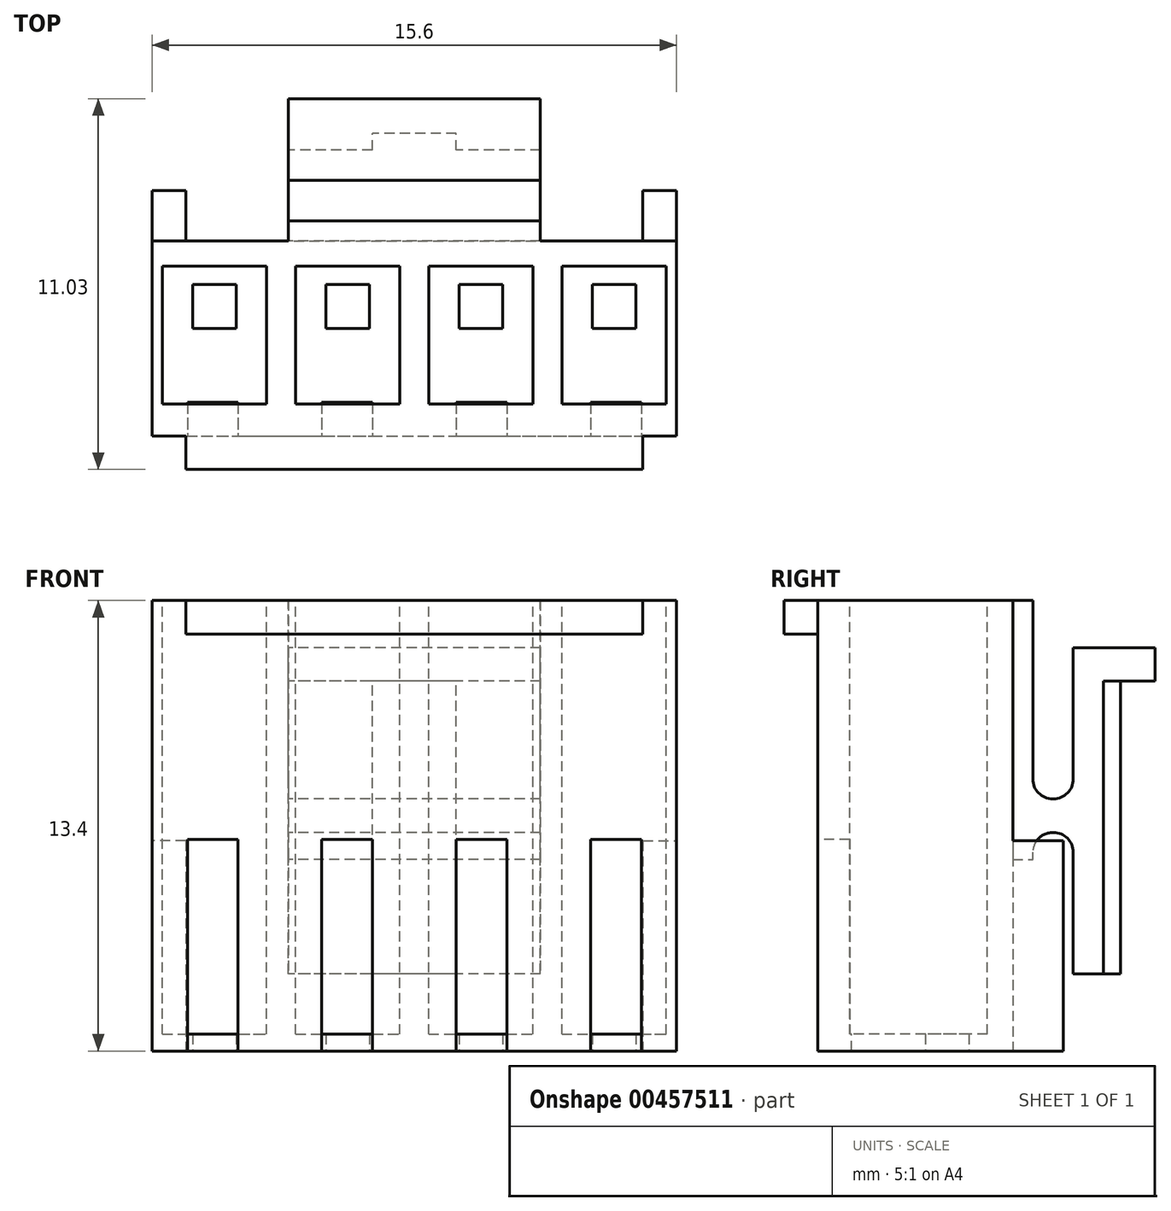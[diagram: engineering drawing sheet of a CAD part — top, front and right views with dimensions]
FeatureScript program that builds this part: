
annotation { "Feature Type Name" : "Feature", "Feature Type Description" : "" }
export const myFeature = defineFeature(function(context is Context, id is Id, definition is map)
    precondition{}
    {
        {
            var Q0;
            Q0=qCreatedBy(makeId("Top.planeOp"),FACE);
            var sketch = newSketch(context, id + "F0", { "sketchPlane" : qUnion([Q0])});
            skLineSegment(sketch, "E0.bottom", {"start": v(-7.8, 2.9) * mm, "end": v(7.8, 2.9) * mm});
            skLineSegment(sketch, "E0.top", {"start": v(-7.8, -2.9) * mm, "end": v(7.8, -2.9) * mm});
            skLineSegment(sketch, "E0.left", {"start": v(-7.8, 2.9) * mm, "end": v(-7.8, -2.9) * mm});
            skLineSegment(sketch, "E0.right", {"start": v(7.8, 2.9) * mm, "end": v(7.8, -2.9) * mm});
            skPoint(sketch, "E0.middle", {"position": v(0, 0) * mm});
            skSolve(sketch);
        }
        {
            var Q0;
            Q0=makeQuery(id+"F0.imprint","IMPRINT",FACE,{"disambiguationData":[TD([[makeQuery(id+"F0.imprint","IMPRINT",EDGE,{"derivedFrom":sQuery(id+"F0.wireOp",EDGE,"E0.bottom")}),-1.0]])]});
            extrude(context, id + "F1", {"entities" : qUnion([Q0]), "depth" : 13.4 * mm});
        }
        {
            var Q0;
            Q0=makeQuery(id+"F1.opExtrude","SWEPT_FACE",FACE,{"disambiguationData":[OSD([sQuery(id+"F0.wireOp",EDGE,"E0.right")])]});
            var sketch = newSketch(context, id + "F2", { "sketchPlane" : qUnion([Q0])});
            skLineSegment(sketch, "E1.bottom", {"start": v(2.9, 0) * mm, "end": v(4.4, 0) * mm});
            skLineSegment(sketch, "E1.top", {"start": v(2.9, 6.25) * mm, "end": v(4.4, 6.25) * mm});
            skLineSegment(sketch, "E1.left", {"start": v(2.9, 0) * mm, "end": v(2.9, 6.25) * mm});
            skLineSegment(sketch, "E1.right", {"start": v(4.4, 0) * mm, "end": v(4.4, 6.25) * mm});
            skSolve(sketch);
        }
        {
            var Q0;
            Q0=makeQuery(id+"F2.imprint","IMPRINT",FACE,{"disambiguationData":[TD([[makeQuery(id+"F2.imprint","IMPRINT",EDGE,{"derivedFrom":sQuery(id+"F2.wireOp",EDGE,"E1.bottom")}),1.0]])]});
            extrude(context, id + "F3", {"entities" : qUnion([Q0]), "operationType" : NewBodyOperationType.ADD, "oppositeDirection" : true, "depth" : 1 * mm});
        }
        {
            var Q0;
            Q0=makeQuery(id+"F1.opExtrude","SWEPT_FACE",FACE,{"disambiguationData":[OSD([sQuery(id+"F0.wireOp",EDGE,"E0.left")])]});
            var sketch = newSketch(context, id + "F4", { "sketchPlane" : qUnion([Q0])});
            skLineSegment(sketch, "E2.bottom", {"start": v(-2.9, 0) * mm, "end": v(-4.4, 0) * mm});
            skLineSegment(sketch, "E2.top", {"start": v(-2.9, 6.25) * mm, "end": v(-4.4, 6.25) * mm});
            skLineSegment(sketch, "E2.left", {"start": v(-2.9, 0) * mm, "end": v(-2.9, 6.25) * mm});
            skLineSegment(sketch, "E2.right", {"start": v(-4.4, 0) * mm, "end": v(-4.4, 6.25) * mm});
            skSolve(sketch);
        }
        {
            var Q0;
            Q0=makeQuery(id+"F4.imprint","IMPRINT",FACE,{"disambiguationData":[TD([[makeQuery(id+"F4.imprint","IMPRINT",EDGE,{"derivedFrom":sQuery(id+"F4.wireOp",EDGE,"E2.bottom")}),-1.0]])]});
            extrude(context, id + "F5", {"entities" : qUnion([Q0]), "operationType" : NewBodyOperationType.ADD, "oppositeDirection" : true, "depth" : 1 * mm});
        }
        {
            var Q0;
            Q0=makeQuery(id+"F1.opExtrude","SWEPT_FACE",FACE,{"disambiguationData":[OSD([sQuery(id+"F0.wireOp",EDGE,"E0.top")])]});
            var sketch = newSketch(context, id + "F6", { "sketchPlane" : qUnion([Q0])});
            skLineSegment(sketch, "E3.bottom", {"start": v(-6.8, 13.4) * mm, "end": v(6.8, 13.4) * mm});
            skLineSegment(sketch, "E3.top", {"start": v(-6.8, 12.4) * mm, "end": v(6.8, 12.4) * mm});
            skLineSegment(sketch, "E3.left", {"start": v(-6.8, 13.4) * mm, "end": v(-6.8, 12.4) * mm});
            skLineSegment(sketch, "E3.right", {"start": v(6.8, 13.4) * mm, "end": v(6.8, 12.4) * mm});
            skSolve(sketch);
        }
        {
            var Q0;
            Q0=makeQuery(id+"F6.imprint","IMPRINT",FACE,{"disambiguationData":[TD([[makeQuery(id+"F6.imprint","IMPRINT",EDGE,{"derivedFrom":sQuery(id+"F6.wireOp",EDGE,"E3.bottom")}),-1.0]])]});
            extrude(context, id + "F7", {"entities" : qUnion([Q0]), "operationType" : NewBodyOperationType.ADD, "depth" : 1 * mm});
        }
        {
            var Q0;
            Q0=makeQuery(id+"F1.opExtrude","SWEPT_FACE",FACE,{"disambiguationData":[OSD([sQuery(id+"F0.wireOp",EDGE,"E0.top")])]});
            var sketch = newSketch(context, id + "F8", { "sketchPlane" : qUnion([Q0])});
            skLineSegment(sketch, "E4.bottom", {"start": v(-6.75, 0) * mm, "end": v(-5.25, 0) * mm});
            skLineSegment(sketch, "E4.top", {"start": v(-6.75, 6.3) * mm, "end": v(-5.25, 6.3) * mm});
            skLineSegment(sketch, "E4.left", {"start": v(-6.75, 0) * mm, "end": v(-6.75, 6.3) * mm});
            skLineSegment(sketch, "E4.right", {"start": v(-5.25, 0) * mm, "end": v(-5.25, 6.3) * mm});
            skLineSegment(sketch, "E5.bottom", {"start": v(-2.75, 0) * mm, "end": v(-1.25, 0) * mm});
            skLineSegment(sketch, "E5.top", {"start": v(-2.75, 6.3) * mm, "end": v(-1.25, 6.3) * mm});
            skLineSegment(sketch, "E5.left", {"start": v(-2.75, 0) * mm, "end": v(-2.75, 6.3) * mm});
            skLineSegment(sketch, "E5.right", {"start": v(-1.25, 0) * mm, "end": v(-1.25, 6.3) * mm});
            skLineSegment(sketch, "E6.bottom", {"start": v(1.25, 0) * mm, "end": v(2.75, 0) * mm});
            skLineSegment(sketch, "E6.top", {"start": v(1.25, 6.3) * mm, "end": v(2.75, 6.3) * mm});
            skLineSegment(sketch, "E6.left", {"start": v(1.25, 0) * mm, "end": v(1.25, 6.3) * mm});
            skLineSegment(sketch, "E6.right", {"start": v(2.75, 0) * mm, "end": v(2.75, 6.3) * mm});
            skLineSegment(sketch, "E7.bottom", {"start": v(5.25, 0) * mm, "end": v(6.75, 0) * mm});
            skLineSegment(sketch, "E7.top", {"start": v(5.25, 6.3) * mm, "end": v(6.75, 6.3) * mm});
            skLineSegment(sketch, "E7.left", {"start": v(5.25, 0) * mm, "end": v(5.25, 6.3) * mm});
            skLineSegment(sketch, "E7.right", {"start": v(6.75, 0) * mm, "end": v(6.75, 6.3) * mm});
            skSolve(sketch);
        }
        {
            var Q0;
            Q0=makeQuery(id+"F8.imprint","IMPRINT",FACE,{"disambiguationData":[TD([[makeQuery(id+"F8.imprint","IMPRINT",EDGE,{"derivedFrom":sQuery(id+"F8.wireOp",EDGE,"E4.bottom")}),1.0]])]});
            var Q1;
            Q1=makeQuery(id+"F8.imprint","IMPRINT",FACE,{"disambiguationData":[TD([[makeQuery(id+"F8.imprint","IMPRINT",EDGE,{"derivedFrom":sQuery(id+"F8.wireOp",EDGE,"E5.bottom")}),1.0]])]});
            var Q2;
            Q2=makeQuery(id+"F8.imprint","IMPRINT",FACE,{"disambiguationData":[TD([[makeQuery(id+"F8.imprint","IMPRINT",EDGE,{"derivedFrom":sQuery(id+"F8.wireOp",EDGE,"E6.bottom")}),1.0]])]});
            var Q3;
            Q3=makeQuery(id+"F8.imprint","IMPRINT",FACE,{"disambiguationData":[TD([[makeQuery(id+"F8.imprint","IMPRINT",EDGE,{"derivedFrom":sQuery(id+"F8.wireOp",EDGE,"E7.bottom")}),1.0]])]});
            extrude(context, id + "F9", {"entities" : qUnion([Q0, Q1, Q2, Q3]), "operationType" : NewBodyOperationType.REMOVE, "oppositeDirection" : true, "depth" : 1 * mm});
        }
        {
            var Q0;
            Q0=qCreatedBy(makeId("Top.planeOp"),FACE);
            var sketch = newSketch(context, id + "F10", { "sketchPlane" : qUnion([Q0])});
            skLineSegment(sketch, "E8.bottom", {"start": v(-1.33, 0.3) * mm, "end": v(-2.63, 0.3) * mm});
            skLineSegment(sketch, "E8.top", {"start": v(-1.33, 1.6) * mm, "end": v(-2.63, 1.6) * mm});
            skLineSegment(sketch, "E8.left", {"start": v(-1.33, 0.3) * mm, "end": v(-1.33, 1.6) * mm});
            skLineSegment(sketch, "E8.right", {"start": v(-2.63, 0.3) * mm, "end": v(-2.63, 1.6) * mm});
            skLineSegment(sketch, "E9.bottom", {"start": v(-5.29, 0.3) * mm, "end": v(-6.6, 0.3) * mm});
            skLineSegment(sketch, "E9.top", {"start": v(-5.29, 1.6) * mm, "end": v(-6.6, 1.6) * mm});
            skLineSegment(sketch, "E9.left", {"start": v(-5.29, 0.3) * mm, "end": v(-5.29, 1.6) * mm});
            skLineSegment(sketch, "E9.right", {"start": v(-6.6, 0.3) * mm, "end": v(-6.6, 1.6) * mm});
            skLineSegment(sketch, "E10.bottom", {"start": v(1.33, 0.3) * mm, "end": v(2.63, 0.3) * mm});
            skLineSegment(sketch, "E10.top", {"start": v(1.33, 1.6) * mm, "end": v(2.63, 1.6) * mm});
            skLineSegment(sketch, "E10.left", {"start": v(1.33, 0.3) * mm, "end": v(1.33, 1.6) * mm});
            skLineSegment(sketch, "E10.right", {"start": v(2.63, 0.3) * mm, "end": v(2.63, 1.6) * mm});
            skLineSegment(sketch, "E11.bottom", {"start": v(5.3, 0.3) * mm, "end": v(6.6, 0.3) * mm});
            skLineSegment(sketch, "E11.top", {"start": v(5.3, 1.6) * mm, "end": v(6.6, 1.6) * mm});
            skLineSegment(sketch, "E11.left", {"start": v(5.3, 0.3) * mm, "end": v(5.3, 1.6) * mm});
            skLineSegment(sketch, "E11.right", {"start": v(6.6, 0.3) * mm, "end": v(6.6, 1.6) * mm});
            skSolve(sketch);
        }
        {
            var Q0;
            Q0=makeQuery(id+"F10.imprint","IMPRINT",FACE,{"disambiguationData":[TD([[makeQuery(id+"F10.imprint","IMPRINT",EDGE,{"derivedFrom":sQuery(id+"F10.wireOp",EDGE,"E11.bottom")}),1.0]])]});
            var Q1;
            Q1=makeQuery(id+"F10.imprint","IMPRINT",FACE,{"disambiguationData":[TD([[makeQuery(id+"F10.imprint","IMPRINT",EDGE,{"derivedFrom":sQuery(id+"F10.wireOp",EDGE,"E10.bottom")}),1.0]])]});
            var Q2;
            Q2=makeQuery(id+"F10.imprint","IMPRINT",FACE,{"disambiguationData":[TD([[makeQuery(id+"F10.imprint","IMPRINT",EDGE,{"derivedFrom":sQuery(id+"F10.wireOp",EDGE,"E8.bottom")}),-1.0]])]});
            var Q3;
            Q3=makeQuery(id+"F10.imprint","IMPRINT",FACE,{"disambiguationData":[TD([[makeQuery(id+"F10.imprint","IMPRINT",EDGE,{"derivedFrom":sQuery(id+"F10.wireOp",EDGE,"E9.bottom")}),-1.0]])]});
            extrude(context, id + "F11", {"entities" : qUnion([Q0, Q1, Q2, Q3]), "operationType" : NewBodyOperationType.REMOVE, "endBound" : BoundingType.THROUGH_ALL, "depth" : 25 * mm});
        }
        {
            var Q0;
            Q0=makeQuery(id+"F7.boolean.opBoolean","MERGE",FACE,{"derivedFrom":[makeQuery(id+"F1.opExtrude","CAP_FACE",FACE,{"disambiguationData":[OSD([sQuery(id+"F0.wireOp",EDGE,"E0.bottom"),sQuery(id+"F0.wireOp",EDGE,"E0.top"),sQuery(id+"F0.wireOp",EDGE,"E0.left"),sQuery(id+"F0.wireOp",EDGE,"E0.right")])],"isStart":false}),makeQuery(id+"F7.opExtrude","SWEPT_FACE",FACE,{"disambiguationData":[OSD([sQuery(id+"F6.wireOp",EDGE,"E3.bottom")])]})]});
            var sketch = newSketch(context, id + "F12", { "sketchPlane" : qUnion([Q0])});
            skLineSegment(sketch, "E12.bottom", {"start": v(-7.49, 2.15) * mm, "end": v(-4.39, 2.15) * mm});
            skLineSegment(sketch, "E12.top", {"start": v(-7.49, -1.95) * mm, "end": v(-4.39, -1.95) * mm});
            skLineSegment(sketch, "E12.left", {"start": v(-7.49, 2.15) * mm, "end": v(-7.49, -1.95) * mm});
            skLineSegment(sketch, "E12.right", {"start": v(-4.39, 2.15) * mm, "end": v(-4.39, -1.95) * mm});
            skLineSegment(sketch, "E13.1.0.0", {"start": v(-3.53, 2.15) * mm, "end": v(-0.43, 2.15) * mm});
            skLineSegment(sketch, "E13.1.0.1", {"start": v(-3.53, 2.15) * mm, "end": v(-3.53, -1.95) * mm});
            skLineSegment(sketch, "E13.1.0.2", {"start": v(-3.53, -1.95) * mm, "end": v(-0.43, -1.95) * mm});
            skLineSegment(sketch, "E13.1.0.3", {"start": v(-0.43, 2.15) * mm, "end": v(-0.43, -1.95) * mm});
            skLineSegment(sketch, "E13.2.0.0", {"start": v(0.43, 2.15) * mm, "end": v(3.53, 2.15) * mm});
            skLineSegment(sketch, "E13.2.0.1", {"start": v(0.43, 2.15) * mm, "end": v(0.43, -1.95) * mm});
            skLineSegment(sketch, "E13.2.0.2", {"start": v(0.43, -1.95) * mm, "end": v(3.53, -1.95) * mm});
            skLineSegment(sketch, "E13.2.0.3", {"start": v(3.53, 2.15) * mm, "end": v(3.53, -1.95) * mm});
            skLineSegment(sketch, "E13.3.0.0", {"start": v(4.4, 2.15) * mm, "end": v(7.5, 2.15) * mm});
            skLineSegment(sketch, "E13.3.0.1", {"start": v(4.4, 2.15) * mm, "end": v(4.4, -1.95) * mm});
            skLineSegment(sketch, "E13.3.0.2", {"start": v(4.4, -1.95) * mm, "end": v(7.5, -1.95) * mm});
            skLineSegment(sketch, "E13.3.0.3", {"start": v(7.5, 2.15) * mm, "end": v(7.5, -1.95) * mm});
            skLineSegment(sketch, "E13.direction1", {"start": v(-7.49, 2.15) * mm, "end": v(-3.53, 2.15) * mm, "construction": true});
            skSolve(sketch);
        }
        {
            var Q0;
            Q0=makeQuery(id+"F12.imprint","IMPRINT",FACE,{"disambiguationData":[TD([[makeQuery(id+"F12.imprint","IMPRINT",EDGE,{"derivedFrom":sQuery(id+"F12.wireOp",EDGE,"E12.bottom")}),-1.0]])]});
            var Q1;
            Q1=makeQuery(id+"F12.imprint","IMPRINT",FACE,{"disambiguationData":[TD([[makeQuery(id+"F12.imprint","IMPRINT",EDGE,{"derivedFrom":sQuery(id+"F12.wireOp",EDGE,"E13.1.0.0")}),-1.0]])]});
            var Q2;
            Q2=makeQuery(id+"F12.imprint","IMPRINT",FACE,{"disambiguationData":[TD([[makeQuery(id+"F12.imprint","IMPRINT",EDGE,{"derivedFrom":sQuery(id+"F12.wireOp",EDGE,"E13.2.0.0")}),-1.0]])]});
            var Q3;
            Q3=makeQuery(id+"F12.imprint","IMPRINT",FACE,{"disambiguationData":[TD([[makeQuery(id+"F12.imprint","IMPRINT",EDGE,{"derivedFrom":sQuery(id+"F12.wireOp",EDGE,"E13.3.0.0")}),-1.0]])]});
            extrude(context, id + "F13", {"entities" : qUnion([Q0, Q1, Q2, Q3]), "operationType" : NewBodyOperationType.REMOVE, "oppositeDirection" : true, "depth" : 12.9 * mm});
        }
        {
            var Q0;
            Q0=qCreatedBy(makeId("Right.planeOp"),FACE);
            var sketch = newSketch(context, id + "F14", { "sketchPlane" : qUnion([Q0])});
            skLineSegment(sketch, "E14", {"start": v(2.9, 13.4) * mm, "end": v(2.9, 5.7) * mm});
            skLineSegment(sketch, "E15", {"start": v(2.9, 5.7) * mm, "end": v(3.5, 5.7) * mm});
            skLineSegment(sketch, "E16", {"start": v(3.5, 5.7) * mm, "end": v(3.5, 5.91) * mm});
            skLineSegment(sketch, "E17", {"start": v(4.1, 6.5) * mm, "end": v(4.11, 6.5) * mm});
            skLineSegment(sketch, "E18", {"start": v(4.7, 5.91) * mm, "end": v(4.7, 2.3) * mm});
            skLineSegment(sketch, "E19", {"start": v(4.7, 2.3) * mm, "end": v(6.1, 2.3) * mm});
            skLineSegment(sketch, "E20", {"start": v(6.1, 2.3) * mm, "end": v(6.1, 11) * mm});
            skLineSegment(sketch, "E21", {"start": v(6.1, 11) * mm, "end": v(7.13, 11) * mm});
            skLineSegment(sketch, "E22", {"start": v(7.13, 11) * mm, "end": v(7.13, 12) * mm});
            skLineSegment(sketch, "E23", {"start": v(7.13, 12) * mm, "end": v(4.7, 12) * mm});
            skLineSegment(sketch, "E24", {"start": v(4.7, 12) * mm, "end": v(4.7, 8.1) * mm});
            skLineSegment(sketch, "E25", {"start": v(4.11, 7.5) * mm, "end": v(4.1, 7.5) * mm});
            skLineSegment(sketch, "E26", {"start": v(3.5, 8.1) * mm, "end": v(3.5, 13.4) * mm});
            skLineSegment(sketch, "E27", {"start": v(3.5, 13.4) * mm, "end": v(2.9, 13.4) * mm});
            skPoint(sketch, "E28.visualSharp", {"position": v(3.5, 6.5) * mm});
            skArc(sketch, "E28.filletArc", {"start": v(4.1, 6.5) * mm, "mid": v(3.67, 6.33) * mm, "end": v(3.5, 5.91) * mm});
            skPoint(sketch, "E29.visualSharp", {"position": v(4.7, 6.5) * mm});
            skArc(sketch, "E29.filletArc", {"start": v(4.7, 5.91) * mm, "mid": v(4.53, 6.33) * mm, "end": v(4.11, 6.5) * mm});
            skPoint(sketch, "E30.visualSharp", {"position": v(3.5, 7.5) * mm});
            skArc(sketch, "E30.filletArc", {"start": v(3.5, 8.1) * mm, "mid": v(3.67, 7.67) * mm, "end": v(4.1, 7.5) * mm});
            skPoint(sketch, "E31.visualSharp", {"position": v(4.7, 7.5) * mm});
            skArc(sketch, "E31.filletArc", {"start": v(4.11, 7.5) * mm, "mid": v(4.53, 7.67) * mm, "end": v(4.7, 8.1) * mm});
            skSolve(sketch);
        }
        {
            var Q0;
            Q0=makeQuery(id+"F14.imprint","IMPRINT",FACE,{"disambiguationData":[TD([[makeQuery(id+"F14.imprint","IMPRINT",EDGE,{"derivedFrom":sQuery(id+"F14.wireOp",EDGE,"E14")}),1.0]])]});
            extrude(context, id + "F15", {"entities" : qUnion([Q0]), "operationType" : NewBodyOperationType.ADD, "depth" : 3.75 * mm, "hasSecondDirection" : true, "secondDirectionOppositeDirection" : true, "secondDirectionDepth" : 3.75 * mm});
        }
        {
            var Q0;
            Q0=makeQuery(id+"F15.opExtrude","SWEPT_FACE",FACE,{"disambiguationData":[OSD([sQuery(id+"F14.wireOp",EDGE,"E20")])]});
            var sketch = newSketch(context, id + "F16", { "sketchPlane" : qUnion([Q0])});
            skLineSegment(sketch, "E32.bottom", {"start": v(-1.25, 2.3) * mm, "end": v(1.25, 2.3) * mm});
            skLineSegment(sketch, "E32.top", {"start": v(-1.25, 11) * mm, "end": v(1.25, 11) * mm});
            skLineSegment(sketch, "E32.left", {"start": v(-1.25, 2.3) * mm, "end": v(-1.25, 11) * mm});
            skLineSegment(sketch, "E32.right", {"start": v(1.25, 2.3) * mm, "end": v(1.25, 11) * mm});
            skSolve(sketch);
        }
        {
            var Q0;
            {var subQ0=sQuery(id+"F16.wireOp",EDGE,"E32.left");Q0=makeQuery(id+"F16.imprint","IMPRINT",FACE,{"disambiguationData":[TD([[makeQuery(id+"F16.imprint","IMPRINT",EDGE,{"derivedFrom":subQ0}),1.0]])]});}
            var Q1;
            {var subQ0=sQuery(id+"F16.wireOp",EDGE,"E32.right");Q1=makeQuery(id+"F16.imprint","IMPRINT",FACE,{"disambiguationData":[TD([[makeQuery(id+"F16.imprint","IMPRINT",EDGE,{"derivedFrom":subQ0}),-1.0]])]});}
            extrude(context, id + "F17", {"entities" : qUnion([Q0, Q1]), "operationType" : NewBodyOperationType.REMOVE, "oppositeDirection" : true, "depth" : 0.5 * mm, "offsetDistance" : 25 * mm});
        }
    });
